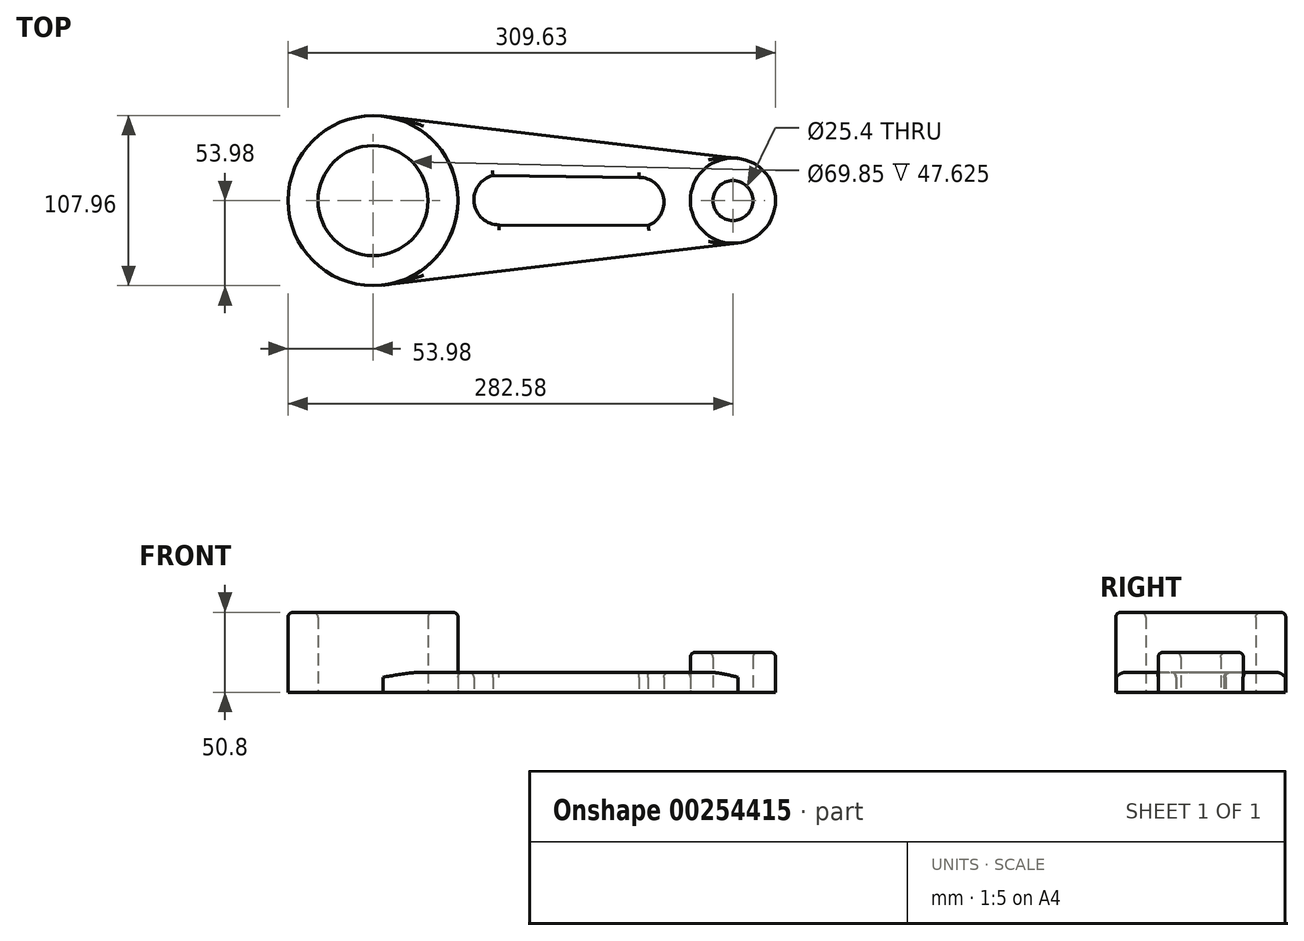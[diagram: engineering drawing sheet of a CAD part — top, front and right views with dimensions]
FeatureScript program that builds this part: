
annotation { "Feature Type Name" : "Feature", "Feature Type Description" : "" }
export const myFeature = defineFeature(function(context is Context, id is Id, definition is map)
    precondition{}
    {
        {
            var Q0;
            Q0=qCreatedBy(makeId("Top.planeOp"),FACE);
            var sketch = newSketch(context, id + "F0", { "sketchPlane" : qUnion([Q0])});
            skLineSegment(sketch, "E0", {"start": v(-44.45, 15.88) * mm, "end": v(48.23, 14.78) * mm});
            skLineSegment(sketch, "E1", {"start": v(-40.67, -15.42) * mm, "end": v(54.03, -15.88) * mm});
            skArc(sketch, "E2", {"start": v(-44.45, 15.88) * mm, "mid": v(-56.43, -1.45) * mm, "end": v(-40.67, -15.42) * mm});
            skArc(sketch, "E3", {"start": v(54.03, -15.87) * mm, "mid": v(63.83, 1.85) * mm, "end": v(48.23, 14.78) * mm});
            skCircle(sketch, "E4", {"center": v(-120.65, 0) * mm, "radius": 34.93 * mm});
            skCircle(sketch, "E5", {"center": v(-120.65, 0) * mm, "radius": 53.98 * mm});
            skCircle(sketch, "E6", {"center": v(107.95, 0) * mm, "radius": 12.7 * mm});
            skCircle(sketch, "E7", {"center": v(107.95, 0) * mm, "radius": 27.05 * mm});
            skLineSegment(sketch, "E8", {"start": v(-114.3, 53.6) * mm, "end": v(111.14, 26.86) * mm});
            skLineSegment(sketch, "E9", {"start": v(-114.3, -53.6) * mm, "end": v(111.14, -26.86) * mm});
            skSolve(sketch);
        }
        {
            var Q0;
            Q0=makeQuery(id+"F0.imprint","IMPRINT",FACE,{"disambiguationData":[TD([[makeQuery(id+"F0.imprint","IMPRINT",EDGE,{"derivedFrom":sQuery(id+"F0.wireOp",EDGE,"E4")}),-1.0]])]});
            extrude(context, id + "F1", {"entities" : qUnion([Q0]), "depth" : 50.8 * mm});
        }
        {
            var Q0;
            Q0=makeQuery(id+"F0.imprint","IMPRINT",FACE,{"disambiguationData":[TD([[makeQuery(id+"F0.imprint","IMPRINT",EDGE,{"derivedFrom":sQuery(id+"F0.wireOp",EDGE,"E6")}),-1.0]])]});
            extrude(context, id + "F2", {"entities" : qUnion([Q0]), "operationType" : NewBodyOperationType.ADD, "depth" : 25.4 * mm});
        }
        {
            var Q0;
            Q0=makeQuery(id+"F0.imprint","IMPRINT",FACE,{"disambiguationData":[TD([[makeQuery(id+"F0.imprint","IMPRINT",EDGE,{"derivedFrom":sQuery(id+"F0.wireOp",EDGE,"E0")}),1.0]])]});
            extrude(context, id + "F3", {"entities" : qUnion([Q0]), "depth" : 12.7 * mm});
        }
        {
            var Q0;
            Q0=makeQuery(id+"F3.opExtrude","CAP_EDGE",EDGE,{"disambiguationData":[OSD([sQuery(id+"F0.wireOp",EDGE,"E9")])],"isStart":false});
            var Q1;
            Q1=makeQuery(id+"F3.opExtrude","CAP_EDGE",EDGE,{"disambiguationData":[OSD([sQuery(id+"F0.wireOp",EDGE,"E1")])],"isStart":false});
            var Q2;
            Q2=makeQuery(id+"F3.opExtrude","CAP_EDGE",EDGE,{"disambiguationData":[OSD([sQuery(id+"F0.wireOp",EDGE,"E0")])],"isStart":false});
            var Q3;
            Q3=makeQuery(id+"F3.opExtrude","CAP_EDGE",EDGE,{"disambiguationData":[OSD([sQuery(id+"F0.wireOp",EDGE,"E3")])],"isStart":false});
            var Q4;
            Q4=makeQuery(id+"F3.opExtrude","CAP_EDGE",EDGE,{"disambiguationData":[OSD([sQuery(id+"F0.wireOp",EDGE,"E2")])],"isStart":false});
            var Q5;
            Q5=makeQuery(id+"F3.opExtrude","CAP_EDGE",EDGE,{"disambiguationData":[OSD([sQuery(id+"F0.wireOp",EDGE,"E8")])],"isStart":false});
            var Q6;
            Q6=makeQuery(id+"F3.opExtrude","CAP_EDGE",EDGE,{"disambiguationData":[OSD([sQuery(id+"F0.wireOp",EDGE,"E5")])],"isStart":false});
            var Q7;
            Q7=makeQuery(id+"F1.opExtrude","CAP_EDGE",EDGE,{"disambiguationData":[OSD([sQuery(id+"F0.wireOp",EDGE,"E4")])],"isStart":false});
            var Q8;
            Q8=makeQuery(id+"F1.opExtrude","CAP_EDGE",EDGE,{"disambiguationData":[OSD([sQuery(id+"F0.wireOp",EDGE,"E5")])],"isStart":false});
            var Q9;
            Q9=makeQuery(id+"F2.opExtrude","CAP_EDGE",EDGE,{"disambiguationData":[OSD([sQuery(id+"F0.wireOp",EDGE,"E7")])],"isStart":false});
            var Q10;
            Q10=makeQuery(id+"F2.opExtrude","CAP_EDGE",EDGE,{"disambiguationData":[OSD([sQuery(id+"F0.wireOp",EDGE,"E6")])],"isStart":false});
            var Q11;
            Q11=makeQuery(id+"F3.opExtrude","CAP_EDGE",EDGE,{"disambiguationData":[OSD([sQuery(id+"F0.wireOp",EDGE,"E7")])],"isStart":false});
            fillet(context, id + "F4", {"entities" : qUnion([Q0, Q1, Q2, Q3, Q4, Q5, Q6, Q7, Q8, Q9, Q10, Q11]), "radius" : 3.17 * mm, "tangentPropagation" : true, "allowEdgeOverflow" : false});
        }
    });
